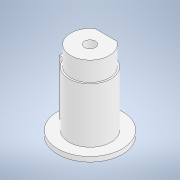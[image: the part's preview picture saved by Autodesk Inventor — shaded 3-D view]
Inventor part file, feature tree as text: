
AUTODESK INVENTOR PART (.ipt)
format: ipt  version: 2020.4 (Build 244396000, 396)  size: 151,552 bytes
history: native  units: mm
features: sketch x5, extrude x4, hole x1
ambient origin geometry x8: Origin, YZ Plane, XZ Plane, XY Plane, X Axis, Y Axis, Z Axis, Center Point
bodies: Solid1 (feature_tree)
feature tree (10):
  extrude  "Extrusion1"  Depth=17.0mm TaperAngle=0.0deg
  extrude  "Extrusion2"  Depth=20.0mm TaperAngle=0.0deg
  extrude  "Extrusion3"  Depth=3.5mm
  hole  "Hole1"  [1 undecoded]
  extrude  "Extrusion4"  Depth=10.0mm
  sketch  "Sketch1"  dims[d0=13.0mm d1=17.0mm d2=0.0mm]
  sketch  "Sketch2"  dims[d3=20.0mm d4=1.5mm d5=0.0mm]
  sketch  "Sketch4"  dims[d8=1.5mm d9=3.5mm]
  sketch  "Sketch5"  dims[d10=12.0mm d11=6.0mm d12=0.0mm]
  sketch  "Sketch6"  dims[d13=3.4mm d14=6.0mm d15=11.0mm d16=2.6mm d17=90.0deg d18=9.0mm d19=20.594885mm d21=2.0mm d24=10.0mm d25=0.0mm d26=3.0mm d27=5.0mm]
note: 1 required parameter value undecoded (feature->parameter linkage not recoverable at this tier; creation-order binding heuristic only, values carry confidence <= 0.55)
